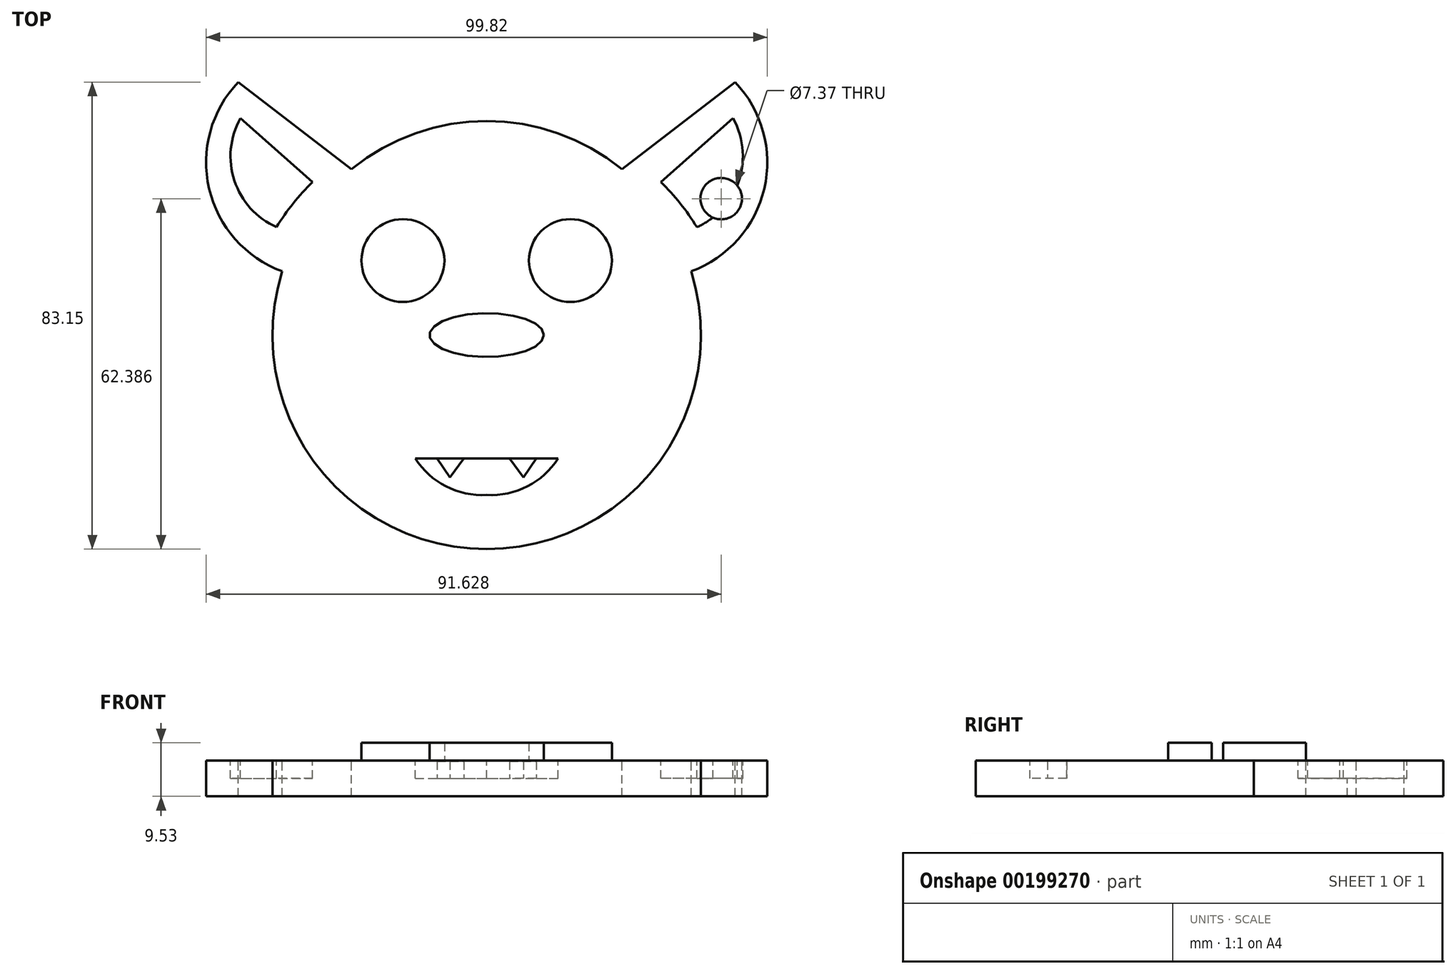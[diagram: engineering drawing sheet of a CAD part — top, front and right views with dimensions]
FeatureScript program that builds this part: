
annotation { "Feature Type Name" : "Feature", "Feature Type Description" : "" }
export const myFeature = defineFeature(function(context is Context, id is Id, definition is map)
    precondition{}
    {
        {
            var Q0;
            Q0=qCreatedBy(makeId("Top.planeOp"),FACE);
            var sketch = newSketch(context, id + "F0", { "sketchPlane" : qUnion([Q0])});
            skCircle(sketch, "E0", {"center": v(0, 0) * mm, "radius": 38.1 * mm});
            skLineSegment(sketch, "E1", {"start": v(24.06, 29.54) * mm, "end": v(44.18, 45.05) * mm});
            skArc(sketch, "E2", {"start": v(36.37, 11.35) * mm, "mid": v(49.37, 26.09) * mm, "end": v(44.18, 45.05) * mm});
            skLineSegment(sketch, "E3.MirrorCS", {"start": v(-24.06, 29.54) * mm, "end": v(-44.18, 45.05) * mm});
            skArc(sketch, "E4.MirrorCS", {"start": v(-36.37, 11.35) * mm, "mid": v(-49.37, 26.09) * mm, "end": v(-44.18, 45.05) * mm});
            skSolve(sketch);
        }
        {
            var Q0;
            Q0 = qSketchRegion(id + "F0", true);
            var Q1;
            Q1 = qSketchRegion(id + "F2", true);
            extrude(context, id + "F1", {"entities" : qUnion([Q0, Q1]), "oppositeDirection" : true, "offsetDistance" : 25.4 * mm, "depth" : 6.35 * mm});
        }
        {
            var Q0;
            Q0=qCreatedBy(makeId("Top.planeOp"),FACE);
            var sketch = newSketch(context, id + "F2", { "sketchPlane" : qUnion([Q0])});
            skEllipse(sketch, "E5", {"center": v(0, 0) * mm, "majorRadius": 10.16 * mm, "minorRadius": 3.88 * mm, "majorAxis": v(1, 0)});
            skSolve(sketch);
        }
        {
            var Q0;
            Q0 = qSketchRegion(id + "F2", true);
            extrude(context, id + "F3", {"entities" : qUnion([Q0]), "operationType" : NewBodyOperationType.ADD, "depth" : 3.17 * mm});
        }
        {
            var Q0;
            Q0=makeQuery(id+"F1.opExtrude","CAP_FACE",FACE,{"disambiguationData":[OSD([sQuery(id+"F0.wireOp",EDGE,"E0"),sQuery(id+"F0.wireOp",EDGE,"E1"),sQuery(id+"F0.wireOp",EDGE,"E2"),sQuery(id+"F0.wireOp",EDGE,"E3.MirrorCS"),sQuery(id+"F0.wireOp",EDGE,"E4.MirrorCS")])],"isStart":true});
            var sketch = newSketch(context, id + "F4", { "sketchPlane" : qUnion([Q0])});
            skCircle(sketch, "E6", {"center": v(-14.9, 13.26) * mm, "radius": 7.38 * mm});
            skCircle(sketch, "E7.MirrorC", {"center": v(14.9, 13.26) * mm, "radius": 7.38 * mm});
            skSolve(sketch);
        }
        {
            var Q0;
            Q0=makeQuery(id+"F1.opExtrude","CAP_FACE",FACE,{"disambiguationData":[OSD([sQuery(id+"F0.wireOp",EDGE,"E0"),sQuery(id+"F0.wireOp",EDGE,"E1"),sQuery(id+"F0.wireOp",EDGE,"E2"),sQuery(id+"F0.wireOp",EDGE,"E3.MirrorCS"),sQuery(id+"F0.wireOp",EDGE,"E4.MirrorCS")])],"isStart":true});
            var sketch = newSketch(context, id + "F5", { "sketchPlane" : qUnion([Q0])});
            skLineSegment(sketch, "E8", {"start": v(-43.8, 38.59) * mm, "end": v(-31, 27.27) * mm});
            skArc(sketch, "E9", {"start": v(-31, 27.27) * mm, "mid": v(-34.43, 23.43) * mm, "end": v(-37.4, 19.22) * mm});
            skPoint(sketch, "E9.endSnap0", {"position": v(-37.4, 32.93) * mm});
            skArc(sketch, "E10", {"start": v(-43.8, 38.59) * mm, "mid": v(-44.88, 27.5) * mm, "end": v(-37.4, 19.22) * mm});
            skPoint(sketch, "E11.MirrorP", {"position": v(37.4, 32.93) * mm});
            skLineSegment(sketch, "E12.MirrorCS", {"start": v(43.8, 38.59) * mm, "end": v(31, 27.27) * mm});
            skArc(sketch, "E13.MirrorCS", {"start": v(43.8, 38.59) * mm, "mid": v(44.88, 27.5) * mm, "end": v(37.4, 19.22) * mm});
            skArc(sketch, "E14.MirrorCS", {"start": v(31, 27.27) * mm, "mid": v(34.43, 23.43) * mm, "end": v(37.4, 19.22) * mm});
            skSolve(sketch);
        }
        {
            var Q0;
            Q0 = qSketchRegion(id + "F5", true);
            extrude(context, id + "F6", {"entities" : qUnion([Q0]), "operationType" : NewBodyOperationType.REMOVE, "oppositeDirection" : true, "depth" : 3.17 * mm});
        }
        {
            var Q0;
            Q0=makeQuery(id+"F1.opExtrude","CAP_FACE",FACE,{"disambiguationData":[OSD([sQuery(id+"F0.wireOp",EDGE,"E0"),sQuery(id+"F0.wireOp",EDGE,"E1"),sQuery(id+"F0.wireOp",EDGE,"E2"),sQuery(id+"F0.wireOp",EDGE,"E3.MirrorCS"),sQuery(id+"F0.wireOp",EDGE,"E4.MirrorCS")])],"isStart":true});
            var sketch = newSketch(context, id + "F7", { "sketchPlane" : qUnion([Q0])});
            skLineSegment(sketch, "E15", {"start": v(0, -21.95) * mm, "end": v(-12.7, -21.95) * mm});
            skLineSegment(sketch, "E16.MirrorCS", {"start": v(0, -21.95) * mm, "end": v(12.7, -21.95) * mm});
            skArc(sketch, "E17", {"start": v(-12.7, -21.95) * mm, "mid": v(-7.24, -26.94) * mm, "end": v(0, -28.46) * mm});
            skArc(sketch, "E18.MirrorCS", {"start": v(12.7, -21.95) * mm, "mid": v(7.24, -26.94) * mm, "end": v(0, -28.46) * mm});
            skSolve(sketch);
        }
        {
            var Q0;
            Q0 = qSketchRegion(id + "F7", true);
            extrude(context, id + "F8", {"entities" : qUnion([Q0]), "operationType" : NewBodyOperationType.REMOVE, "oppositeDirection" : true, "depth" : 3.17 * mm});
        }
        {
            var Q0;
            Q0=makeQuery(id+"F8.boolean.opBoolean","COPY",FACE,{"derivedFrom":makeQuery(id+"F8.opExtrude","CAP_FACE",FACE,{"disambiguationData":[OSD([sQuery(id+"F7.wireOp",EDGE,"E15"),sQuery(id+"F7.wireOp",EDGE,"E16.MirrorCS"),sQuery(id+"F7.wireOp",EDGE,"E17"),sQuery(id+"F7.wireOp",EDGE,"E18.MirrorCS")])],"isStart":false})});
            var sketch = newSketch(context, id + "F9", { "sketchPlane" : qUnion([Q0])});
            skLineSegment(sketch, "E19", {"start": v(-8.82, -21.95) * mm, "end": v(-6.54, -25.33) * mm});
            skLineSegment(sketch, "E20", {"start": v(-6.54, -25.33) * mm, "end": v(-4.07, -21.95) * mm});
            skLineSegment(sketch, "E21.MirrorCS", {"start": v(6.54, -25.33) * mm, "end": v(4.07, -21.95) * mm});
            skLineSegment(sketch, "E22.MirrorCS", {"start": v(8.82, -21.95) * mm, "end": v(6.54, -25.33) * mm});
            skLineSegment(sketch, "E23", {"start": v(-8.82, -21.95) * mm, "end": v(-4.07, -21.95) * mm});
            skLineSegment(sketch, "E24.MirrorCS", {"start": v(8.82, -21.95) * mm, "end": v(4.07, -21.95) * mm});
            skSolve(sketch);
        }
        {
            var Q0;
            Q0 = qSketchRegion(id + "F9", true);
            extrude(context, id + "F10", {"entities" : qUnion([Q0]), "operationType" : NewBodyOperationType.ADD, "depth" : 3.05 * mm});
        }
        {
            var Q0;
            Q0 = qSketchRegion(id + "F4", true);
            extrude(context, id + "F11", {"entities" : qUnion([Q0]), "operationType" : NewBodyOperationType.ADD, "depth" : 3.17 * mm});
        }
        {
            var Q0;
            Q0=makeQuery(id+"F4.imprint","IMPRINT",FACE,{"disambiguationData":[TD([[makeQuery(id+"F4.imprint","IMPRINT",EDGE,{"derivedFrom":sQuery(id+"F4.wireOp",EDGE,"E6")}),-1.0]])]});
            var sketch = newSketch(context, id + "F12", { "sketchPlane" : qUnion([Q0])});
            skCircle(sketch, "E25", {"center": v(41.72, 24.29) * mm, "radius": 3.69 * mm});
            skSolve(sketch);
        }
        {
            var Q0;
            Q0 = qSketchRegion(id + "F12", true);
            extrude(context, id + "F13", {"entities" : qUnion([Q0]), "operationType" : NewBodyOperationType.REMOVE, "endBound" : BoundingType.THROUGH_ALL, "oppositeDirection" : true, "depth" : 25.4 * mm});
        }
    });
